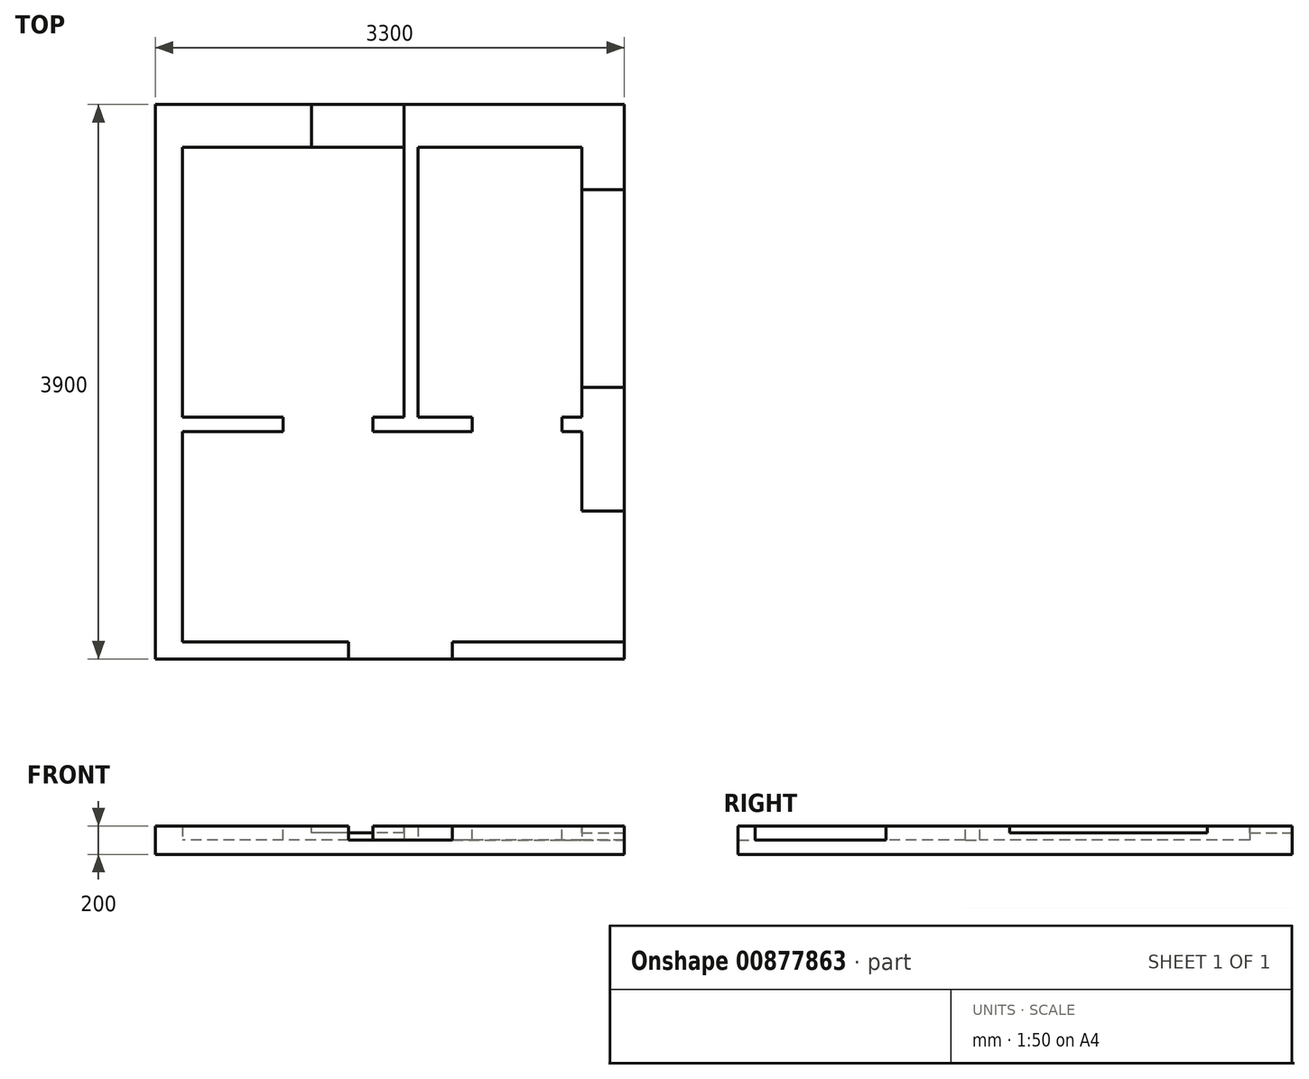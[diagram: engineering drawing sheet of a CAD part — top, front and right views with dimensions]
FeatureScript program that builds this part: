
annotation { "Feature Type Name" : "Feature", "Feature Type Description" : "" }
export const myFeature = defineFeature(function(context is Context, id is Id, definition is map)
    precondition{}
    {
        {
            var Q0;
            Q0=qCreatedBy(makeId("Top.planeOp"),FACE);
            var sketch = newSketch(context, id + "F0", { "sketchPlane" : qUnion([Q0])});
            skLineSegment(sketch, "E0.bottom", {"start": v(0, 0) * mm, "end": v(-3300, 0) * mm});
            skLineSegment(sketch, "E0.top", {"start": v(0, -3900) * mm, "end": v(-3300, -3900) * mm});
            skLineSegment(sketch, "E0.left", {"start": v(0, 0) * mm, "end": v(0, -3900) * mm});
            skLineSegment(sketch, "E0.right", {"start": v(-3300, 0) * mm, "end": v(-3300, -3900) * mm});
            skSolve(sketch);
        }
        {
            var Q0;
            Q0 = qSketchRegion(id + "F0", true);
            extrude(context, id + "F1", {"entities" : qUnion([Q0]), "oppositeDirection" : true, "depth" : 100 * mm, "offsetDistance" : 25 * mm});
        }
        {
            var Q0;
            Q0=makeQuery(id+"F0.imprint","IMPRINT",FACE,{"disambiguationData":[TD([[makeQuery(id+"F0.imprint","IMPRINT",EDGE,{"derivedFrom":sQuery(id+"F0.wireOp",EDGE,"E0.bottom")}),1.0]])]});
            var sketch = newSketch(context, id + "F2", { "sketchPlane" : qUnion([Q0])});
            skLineSegment(sketch, "E1.bottom", {"start": v(-300, -300) * mm, "end": v(-1450, -300) * mm});
            skLineSegment(sketch, "E1.top", {"start": v(-300, -2200) * mm, "end": v(-1450, -2200) * mm});
            skLineSegment(sketch, "E1.left", {"start": v(-300, -300) * mm, "end": v(-300, -2200) * mm});
            skLineSegment(sketch, "E1.right", {"start": v(-1450, -300) * mm, "end": v(-1450, -2200) * mm});
            skLineSegment(sketch, "E2.bottom", {"start": v(-1550, -300) * mm, "end": v(-3110, -300) * mm});
            skLineSegment(sketch, "E2.top", {"start": v(-1550, -2200) * mm, "end": v(-3110, -2200) * mm});
            skLineSegment(sketch, "E2.left", {"start": v(-1550, -300) * mm, "end": v(-1550, -2200) * mm});
            skLineSegment(sketch, "E2.right", {"start": v(-3110, -300) * mm, "end": v(-3110, -2200) * mm});
            skLineSegment(sketch, "E3.bottom", {"start": v(-3110, -2300) * mm, "end": v(-300, -2300) * mm});
            skLineSegment(sketch, "E3.top", {"start": v(-3110, -3780) * mm, "end": v(-300, -3780) * mm});
            skLineSegment(sketch, "E3.left", {"start": v(-3110, -2300) * mm, "end": v(-3110, -3780) * mm});
            skLineSegment(sketch, "E3.right", {"start": v(-300, -2300) * mm, "end": v(-300, -3780) * mm});
            skLineSegment(sketch, "E4.bottom", {"start": v(0, 0) * mm, "end": v(-3300, 0) * mm});
            skLineSegment(sketch, "E4.top", {"start": v(0, -3900) * mm, "end": v(-3300, -3900) * mm});
            skLineSegment(sketch, "E4.left", {"start": v(0, 0) * mm, "end": v(0, -3900) * mm});
            skLineSegment(sketch, "E4.right", {"start": v(-3300, 0) * mm, "end": v(-3300, -3900) * mm});
            skSolve(sketch);
        }
        {
            var Q0;
            Q0 = qSketchRegion(id + "F2", true);
            extrude(context, id + "F3", {"entities" : qUnion([Q0]), "operationType" : NewBodyOperationType.ADD, "depth" : 100 * mm, "offsetDistance" : 25 * mm});
        }
        {
            var Q0;
            Q0=makeQuery(id+"F3.opExtrude","CAP_FACE",FACE,{"disambiguationData":[OSD([sQuery(id+"F2.wireOp",EDGE,"E1.bottom"),sQuery(id+"F2.wireOp",EDGE,"E1.top"),sQuery(id+"F2.wireOp",EDGE,"E1.left"),sQuery(id+"F2.wireOp",EDGE,"E1.right"),sQuery(id+"F2.wireOp",EDGE,"E2.bottom"),sQuery(id+"F2.wireOp",EDGE,"E2.top"),sQuery(id+"F2.wireOp",EDGE,"E2.left"),sQuery(id+"F2.wireOp",EDGE,"E2.right"),sQuery(id+"F2.wireOp",EDGE,"E3.bottom"),sQuery(id+"F2.wireOp",EDGE,"E3.top"),sQuery(id+"F2.wireOp",EDGE,"E3.left"),sQuery(id+"F2.wireOp",EDGE,"E3.right"),sQuery(id+"F2.wireOp",EDGE,"E4.bottom"),sQuery(id+"F2.wireOp",EDGE,"E4.top"),sQuery(id+"F2.wireOp",EDGE,"E4.left"),sQuery(id+"F2.wireOp",EDGE,"E4.right")])],"isStart":false});
            var sketch = newSketch(context, id + "F4", { "sketchPlane" : qUnion([Q0])});
            skLineSegment(sketch, "E5.bottom", {"start": v(-1550, -300) * mm, "end": v(-2200, -300) * mm});
            skLineSegment(sketch, "E5.top", {"start": v(-1550, 0) * mm, "end": v(-2200, 0) * mm});
            skLineSegment(sketch, "E5.left", {"start": v(-1550, -300) * mm, "end": v(-1550, 0) * mm});
            skLineSegment(sketch, "E5.right", {"start": v(-2200, -300) * mm, "end": v(-2200, 0) * mm});
            skLineSegment(sketch, "E6.bottom", {"start": v(-300, -600) * mm, "end": v(0, -600) * mm});
            skLineSegment(sketch, "E6.top", {"start": v(-300, -1990) * mm, "end": v(0, -1990) * mm});
            skLineSegment(sketch, "E6.left", {"start": v(-300, -600) * mm, "end": v(-300, -1990) * mm});
            skLineSegment(sketch, "E6.right", {"start": v(0, -600) * mm, "end": v(0, -1990) * mm});
            skLineSegment(sketch, "E7.bottom", {"start": v(-440, -2200) * mm, "end": v(-1070, -2200) * mm});
            skLineSegment(sketch, "E7.top", {"start": v(-440, -2300) * mm, "end": v(-1070, -2300) * mm});
            skLineSegment(sketch, "E7.left", {"start": v(-440, -2200) * mm, "end": v(-440, -2300) * mm});
            skLineSegment(sketch, "E7.right", {"start": v(-1070, -2200) * mm, "end": v(-1070, -2300) * mm});
            skLineSegment(sketch, "E8.bottom", {"start": v(-1770, -2200) * mm, "end": v(-2400, -2200) * mm});
            skLineSegment(sketch, "E8.top", {"start": v(-1770, -2300) * mm, "end": v(-2400, -2300) * mm});
            skLineSegment(sketch, "E8.left", {"start": v(-1770, -2200) * mm, "end": v(-1770, -2300) * mm});
            skLineSegment(sketch, "E8.right", {"start": v(-2400, -2200) * mm, "end": v(-2400, -2300) * mm});
            skLineSegment(sketch, "E9.bottom", {"start": v(-1210, -3780) * mm, "end": v(-1940, -3780) * mm});
            skLineSegment(sketch, "E9.top", {"start": v(-1210, -3900) * mm, "end": v(-1940, -3900) * mm});
            skLineSegment(sketch, "E9.left", {"start": v(-1210, -3780) * mm, "end": v(-1210, -3900) * mm});
            skLineSegment(sketch, "E9.right", {"start": v(-1940, -3780) * mm, "end": v(-1940, -3900) * mm});
            skLineSegment(sketch, "E10.bottom", {"start": v(-300, -2860) * mm, "end": v(0, -2860) * mm});
            skLineSegment(sketch, "E10.top", {"start": v(-300, -3780) * mm, "end": v(0, -3780) * mm});
            skLineSegment(sketch, "E10.left", {"start": v(-300, -2860) * mm, "end": v(-300, -3780) * mm});
            skLineSegment(sketch, "E10.right", {"start": v(0, -2860) * mm, "end": v(0, -3780) * mm});
            skSolve(sketch);
        }
        {
            var Q0;
            Q0=makeQuery(id+"F4.imprint","IMPRINT",FACE,{"disambiguationData":[TD([[makeQuery(id+"F4.imprint","IMPRINT",EDGE,{"derivedFrom":sQuery(id+"F4.wireOp",EDGE,"E8.bottom")}),1.0]])]});
            var Q1;
            Q1=makeQuery(id+"F4.imprint","IMPRINT",FACE,{"disambiguationData":[TD([[makeQuery(id+"F4.imprint","IMPRINT",EDGE,{"derivedFrom":sQuery(id+"F4.wireOp",EDGE,"E7.bottom")}),1.0]])]});
            var Q2;
            Q2=makeQuery(id+"F4.imprint","IMPRINT",FACE,{"disambiguationData":[TD([[makeQuery(id+"F4.imprint","IMPRINT",EDGE,{"derivedFrom":sQuery(id+"F4.wireOp",EDGE,"E10.bottom")}),-1.0]])]});
            var Q3;
            Q3=makeQuery(id+"F4.imprint","IMPRINT",FACE,{"disambiguationData":[TD([[makeQuery(id+"F4.imprint","IMPRINT",EDGE,{"derivedFrom":sQuery(id+"F4.wireOp",EDGE,"E9.bottom")}),-1.0]])]});
            var Q4;
            Q4=makeQuery(id+"F3.boolean.opBoolean","SPLIT",FACE,{"disambiguationData":[TD([makeQuery(id+"F3.opExtrude","SWEPT_FACE",FACE,{"disambiguationData":[OSD([sQuery(id+"F2.wireOp",EDGE,"E3.bottom")])]})])],"derivedFrom":makeQuery(id+"F1.opExtrude","CAP_FACE",FACE,{"disambiguationData":[OSD([sQuery(id+"F0.wireOp",EDGE,"E0.bottom"),sQuery(id+"F0.wireOp",EDGE,"E0.top"),sQuery(id+"F0.wireOp",EDGE,"E0.left"),sQuery(id+"F0.wireOp",EDGE,"E0.right")])],"isStart":true})});
            extrude(context, id + "F5", {"entities" : qUnion([Q0, Q1, Q2, Q3]), "operationType" : NewBodyOperationType.REMOVE, "endBound" : BoundingType.UP_TO_SURFACE, "oppositeDirection" : true, "depth" : 25 * mm, "endBoundEntityFace" : qUnion([Q4]), "offsetDistance" : 25 * mm});
        }
        {
            var Q0;
            Q0=makeQuery(id+"F4.imprint","IMPRINT",FACE,{"disambiguationData":[TD([[makeQuery(id+"F4.imprint","IMPRINT",EDGE,{"derivedFrom":sQuery(id+"F4.wireOp",EDGE,"E5.bottom")}),-1.0]])]});
            var Q1;
            Q1=makeQuery(id+"F4.imprint","IMPRINT",FACE,{"disambiguationData":[TD([[makeQuery(id+"F4.imprint","IMPRINT",EDGE,{"derivedFrom":sQuery(id+"F4.wireOp",EDGE,"E6.bottom")}),-1.0]])]});
            extrude(context, id + "F6", {"entities" : qUnion([Q0, Q1]), "operationType" : NewBodyOperationType.REMOVE, "oppositeDirection" : true, "depth" : 50 * mm, "offsetDistance" : 25 * mm});
        }
    });
